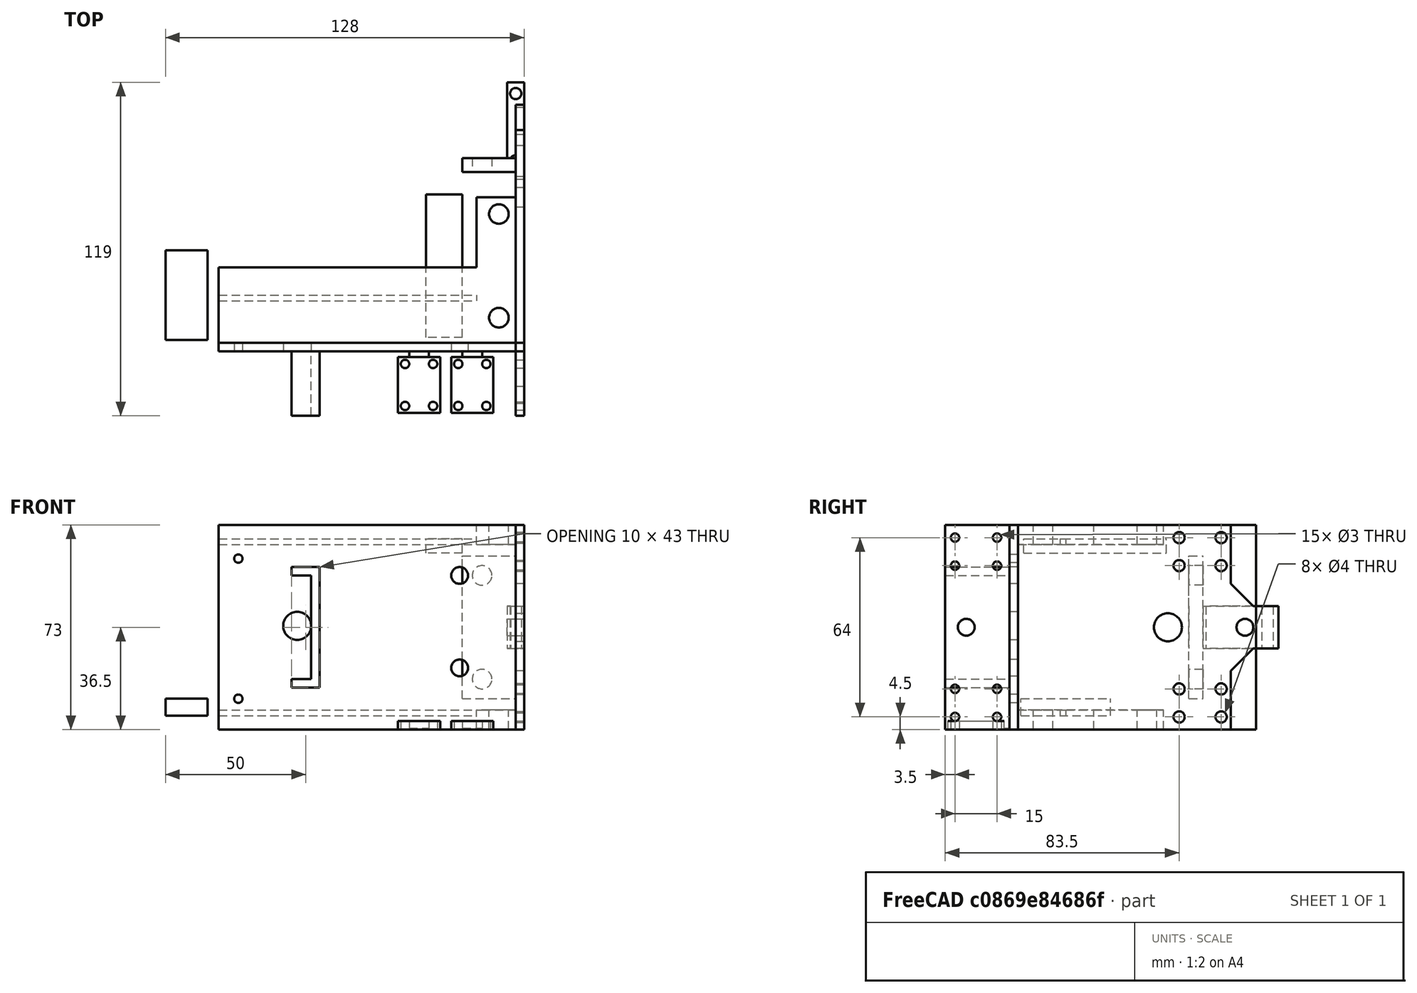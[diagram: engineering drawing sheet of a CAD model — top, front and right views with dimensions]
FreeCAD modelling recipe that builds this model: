
FCSTD DOCUMENT  (FreeCAD 0.16R6703 (Git))
Label: print
License: All rights reserved
LicenseURL: http://en.wikipedia.org/wiki/All_rights_reserved
objects: Part::Cut×48, Part::Cylinder×46, Part::Box×23, Part::MultiFuse×15
note: 132 computed .brp shape members not serialized (recipe doc carries the construction recipe); baked Part::Feature solids carry a one-line shape summary decoded from their .brp

FEATURE [Part::Box] Box001  label="Cube001"
  Height = 73
  Length = 133
  Placement = pos=(-4.99998,-4,-4.99998) rot=(0,0,1;0rad)
  Width = 3
FEATURE [Part::Box] Box005  label="Cube005"
  Height = 7
  Length = 113
  Placement = pos=(0,-4,-5) rot=(0,0,1;0rad)
  Width = 30
FEATURE [Part::Box] Box006  label="Cube006"
  Height = 7
  Length = 113
  Placement = pos=(0,-4,61) rot=(0,0,1;0rad)
  Width = 30
FEATURE [Part::Box] Box007  label="Cube007"
  Height = 2
  Length = 113
  Placement = pos=(0,14,0) rot=(0,0,1;0rad)
  Width = 2
FEATURE [Part::Box] Box008  label="Cube008"
  Height = 2
  Length = 113
  Placement = pos=(0,14,61) rot=(0,0,1;0rad)
  Width = 2
FEATURE [Part::Cut] Cut
  Base = -> Box006
  Tool = -> Box008
FEATURE [Part::Cut] Cut001
  Base = -> Box005
  Tool = -> Box007
FEATURE [Part::Box] Box009  label="Cube009"
  Height = 7
  Length = 55
  Placement = pos=(128,-4,61) rot=(0,0,1;1.5708rad)
  Width = 17
FEATURE [Part::Box] Box013  label="Cube013"
  Height = 7
  Length = 55
  Placement = pos=(128,-4,-5) rot=(0,0,1;1.5708rad)
  Width = 17
FEATURE [Part::Cylinder] Cylinder013
  Angle = 360
  Height = 3
  Placement = pos=(105,-1,50) rot=(1,0,0;1.5708rad)
  Radius = 3
FEATURE [Part::Cylinder] Cylinder015
  Angle = 360
  Height = 3
  Placement = pos=(105,-1,17) rot=(1,0,0;1.5708rad)
  Radius = 3
FEATURE [Part::Cut] Cut014
  Base = -> Box001
  Tool = -> Cylinder013
FEATURE [Part::Cut] Cut015
  Base = -> Cut014
  Tool = -> Cylinder015
FEATURE [Part::Cylinder] Cylinder016
  Angle = 360
  Height = 4
  Placement = pos=(118,-20,63) rot=(0,1,0;1.5708rad)
  Radius = 1.5
FEATURE [Part::Cut] Cut017
  Base = -> Cut015
  Tool = -> Cylinder016
FEATURE [Part::Box] Box  label="Cube"
  Height = 6
  Length = 15
  Width = 32
FEATURE [Part::Box] Box014  label="main_base"
  Height = 73
  Length = 111
  Placement = pos=(128,-27,-5) rot=(0,0,1;1.5708rad)
  Width = 3
FEATURE [Part::Box] Box016  label="Cube016"
  Height = 15
  Length = 20
  Placement = pos=(147,-26,51) rot=(0,0,1;1.5708rad)
  Width = 3
FEATURE [Part::Cylinder] Cylinder
  Angle = 360
  Height = 3
  Placement = pos=(125,-8.5,-0.5) rot=(0,1,0;1.5708rad)
  Radius = 1.5
FEATURE [Part::Cylinder] Cylinder017
  Angle = 360
  Height = 3
  Placement = pos=(125,-8.5,9.5) rot=(0,1,0;1.5708rad)
  Radius = 1.5
FEATURE [Part::Cylinder] Cylinder018
  Angle = 360
  Height = 3
  Placement = pos=(125,-23.5,9.5) rot=(0,1,0;1.5708rad)
  Radius = 1.5
FEATURE [Part::Cylinder] Cylinder019
  Angle = 360
  Height = 3
  Placement = pos=(125,-23.5,-0.5) rot=(0,1,0;1.5708rad)
  Radius = 1.5
FEATURE [Part::Cylinder] Cylinder020
  Angle = 360
  Height = 3
  Placement = pos=(125,-8.5,63.5) rot=(0,1,0;1.5708rad)
  Radius = 1.5
FEATURE [Part::Cylinder] Cylinder021
  Angle = 360
  Height = 3
  Placement = pos=(125,-23.5,53.5) rot=(0,1,0;1.5708rad)
  Radius = 1.5
FEATURE [Part::Cylinder] Cylinder022
  Angle = 360
  Height = 3
  Placement = pos=(125,-8.5,53.5) rot=(0,1,0;1.5708rad)
  Radius = 1.5
FEATURE [Part::Cylinder] Cylinder023
  Angle = 360
  Height = 3
  Placement = pos=(144,-23.5,63.5) rot=(0,1,0;1.5708rad)
  Radius = 1.5
FEATURE [Part::Cylinder] Cylinder024
  Angle = 360
  Height = 3
  Placement = pos=(125,-23.5,63.5) rot=(0,1,0;1.5708rad)
  Radius = 1.5
FEATURE [Part::Cylinder] Cylinder025
  Angle = 360
  Height = 3
  Placement = pos=(144,-8.5,63.5) rot=(0,1,0;1.5708rad)
  Radius = 1.5
FEATURE [Part::Cylinder] Cylinder026
  Angle = 360
  Height = 3
  Placement = pos=(144,-23.5,53.5) rot=(0,1,0;1.5708rad)
  Radius = 1.5
FEATURE [Part::Cylinder] Cylinder027
  Angle = 360
  Height = 3
  Placement = pos=(144,-8.5,53.5) rot=(0,1,0;1.5708rad)
  Radius = 1.5
FEATURE [Part::Cut] Cut018
  Base = -> Box016
  Tool = -> Cylinder027
FEATURE [Part::Cut] Cut019
  Base = -> Cut018
  Tool = -> Cylinder026
FEATURE [Part::Cut] Cut020
  Base = -> Cut019
  Tool = -> Cylinder025
FEATURE [Part::Cut] Cut021  label="motor_mount1"
  Base = -> Cut020
  Placement = pos=(32,0,142) rot=(0,1,0;1.5708rad)
  Tool = -> Cylinder023
FEATURE [Part::Box] Box017  label="Cube017"
  Height = 15
  Length = 20
  Placement = pos=(147,-26,51) rot=(0,0,1;1.5708rad)
  Width = 3
FEATURE [Part::Cylinder] Cylinder028
  Angle = 360
  Height = 3
  Placement = pos=(144,-23.5,63.5) rot=(0,1,0;1.5708rad)
  Radius = 1.5
FEATURE [Part::Cylinder] Cylinder029
  Angle = 360
  Height = 3
  Placement = pos=(144,-8.5,63.5) rot=(0,1,0;1.5708rad)
  Radius = 1.5
FEATURE [Part::Cylinder] Cylinder030
  Angle = 360
  Height = 3
  Placement = pos=(144,-23.5,53.5) rot=(0,1,0;1.5708rad)
  Radius = 1.5
FEATURE [Part::Cylinder] Cylinder031
  Angle = 360
  Height = 3
  Placement = pos=(144,-8.5,53.5) rot=(0,1,0;1.5708rad)
  Radius = 1.5
FEATURE [Part::Cut] Cut022
  Base = -> Box017
  Tool = -> Cylinder031
FEATURE [Part::Cut] Cut023
  Base = -> Cut022
  Tool = -> Cylinder030
FEATURE [Part::Cut] Cut024
  Base = -> Cut023
  Tool = -> Cylinder029
FEATURE [Part::Cut] Cut026
  Base = -> Box014
  Tool = -> Cylinder
FEATURE [Part::Cut] Cut027
  Base = -> Cut026
  Tool = -> Cylinder017
FEATURE [Part::Cut] Cut028
  Base = -> Cut027
  Tool = -> Cylinder018
FEATURE [Part::Cut] Cut029
  Base = -> Cut028
  Tool = -> Cylinder019
FEATURE [Part::Cut] Cut030
  Base = -> Cut029
  Tool = -> Cylinder020
FEATURE [Part::Box] Box018  label="Cube018"
  Height = 43
  Length = 32
  Placement = pos=(55,-33,10) rot=(0,0,1;1.5708rad)
  Width = 10
FEATURE [Part::Box] Box019  label="Cube019"
  Height = 37
  Length = 29
  Placement = pos=(52,-30,13) rot=(0,0,1;1.5708rad)
  Width = 7
FEATURE [Part::Cylinder] Cylinder032
  Angle = 360
  Height = 3
  Placement = pos=(26,-1,6) rot=(1,0,0;1.5708rad)
  Radius = 1.5
FEATURE [Part::Cylinder] Cylinder033
  Angle = 360
  Height = 3
  Placement = pos=(26,-1,56) rot=(1,0,0;1.5708rad)
  Radius = 1.5
FEATURE [Part::Cut] Cut035
  Base = -> Cut017
  Tool = -> Cylinder033
FEATURE [Part::Cut] Cut036  label="chassi_back"
  Base = -> Cut035
  Tool = -> Cylinder032
FEATURE [Part::Box] Box022  label="Cube022"
  Height = 6
  Length = 15
  Width = 32
FEATURE [Part::Cylinder] Cylinder035
  Angle = 360
  Height = 18
  Placement = pos=(0,4,3) rot=(0,1,0;1.5708rad)
  Radius = 2
FEATURE [Part::Cylinder] Cylinder036
  Angle = 360
  Height = 18
  Placement = pos=(0,28,3) rot=(0,1,0;1.5708rad)
  Radius = 2
FEATURE [Part::Cut] Cut039
  Base = -> Box022
  Tool = -> Cylinder035
FEATURE [Part::Cut] Cut040
  Base = -> Cut039
  Placement = pos=(122,60,39) rot=(0,1,0;1.5708rad)
  Tool = -> Cylinder036
FEATURE [Part::MultiFuse] Fusion  label="right_mount"
  Shapes = -> [Cut,Box009]
FEATURE [Part::MultiFuse] Fusion001  label="left_mount"
  Shapes = -> [Cut001,Box013]
FEATURE [Part::Cylinder] Cylinder037
  Angle = 360
  Height = 3
  Placement = pos=(125,-16,21) rot=(0,1,0;1.5708rad)
  Radius = 4
FEATURE [Part::Cylinder] Cylinder038
  Angle = 360
  Height = 3
  Placement = pos=(125,-16,38) rot=(0,1,0;1.5708rad)
  Radius = 4
FEATURE [Part::Cut] Cut041
  Tool = -> Cylinder037
FEATURE [Part::Cut] Cut042
  Base = -> Cut041
  Tool = -> Cylinder038
FEATURE [Part::Cylinder] Cylinder039
  Angle = 360
  Height = 6
  Placement = pos=(122,80,31.5) rot=(0,1,0;1.5708rad)
  Radius = 3
FEATURE [Part::Cut] Cut034  label="battery_holder"
  Base = -> Box018
  Tool = -> Box019
FEATURE [Part::Cylinder] Cylinder040
  Angle = 360
  Height = 3
  Placement = pos=(47,-1,32) rot=(1,0,0;1.5708rad)
  Radius = 5
FEATURE [Part::Cut] Cut044  label="chassi_back001"
  Base = -> Cut036
  Tool = -> Cylinder040
FEATURE [Part::Cylinder] Cylinder041
  Angle = 360
  Height = 7
  Placement = pos=(119,8,61) rot=(0,0,1;0rad)
  Radius = 3.5
FEATURE [Part::Cylinder] Cylinder042
  Angle = 360
  Height = 7
  Placement = pos=(119,45,61) rot=(0,0,1;0rad)
  Radius = 3.5
FEATURE [Part::Cylinder] Cylinder043
  Angle = 360
  Height = 7
  Placement = pos=(119,8,-5) rot=(0,0,1;0rad)
  Radius = 3.5
FEATURE [Part::Cylinder] Cylinder044
  Angle = 360
  Height = 7
  Placement = pos=(119,45,-5) rot=(0,0,1;0rad)
  Radius = 3.5
FEATURE [Part::Cut] Cut045
  Base = -> Fusion
  Tool = -> Cylinder041
FEATURE [Part::Cut] Cut046  label="left_mount001"
  Base = -> Cut045
  Tool = -> Cylinder042
FEATURE [Part::Cut] Cut047
  Base = -> Fusion001
  Tool = -> Cylinder043
FEATURE [Part::Cut] Cut048  label="right_mount001"
  Base = -> Cut047
  Tool = -> Cylinder044
FEATURE [Part::Cylinder] Cylinder046
  Angle = 360
  Height = 7
  Placement = pos=(119,8,61) rot=(0,0,1;0rad)
  Radius = 3.5
FEATURE [Part::Cylinder] Cylinder047
  Angle = 360
  Height = 7
  Placement = pos=(119,45,61) rot=(0,0,1;0rad)
  Radius = 3.5
FEATURE [Part::Box] Box023  label="Cube023"
  Height = 5
  Length = 51
  Placement = pos=(106,1,58) rot=(0,0,1;1.5708rad)
  Width = 13
FEATURE [Part::Box] Box024  label="Cube024"
  Height = 5
  Length = 22
  Placement = pos=(112,1,63) rot=(0,0,1;0rad)
  Width = 51
FEATURE [Part::Cylinder] Cylinder048
  Angle = 360
  Height = 10
  Placement = pos=(119,45,58) rot=(0,0,1;0rad)
  Radius = 3.5
FEATURE [Part::Cylinder] Cylinder049
  Angle = 360
  Height = 10
  Placement = pos=(119,8,58) rot=(0,0,1;0rad)
  Radius = 3.5
FEATURE [Part::Cut] Cut049
  Base = -> Box024
  Tool = -> Cylinder048
FEATURE [Part::Cut] Cut050
  Base = -> Cut049
  Placement = pos=(-6,128,5) rot=(1,0,0;1.5708rad)
  Tool = -> Cylinder049
FEATURE [Part::MultiFuse] Fusion006
  Shapes = -> [Cut034,Cut044]
FEATURE [Part::Box] Box025  label="Cube025"
  Height = 79
  Length = 29
  Placement = pos=(-10,-4,-8) rot=(0,0,1;0rad)
  Width = 30
FEATURE [Part::Cut] Cut025  label="motor_mount2"
  Base = -> Cut024
  Placement = pos=(51,0,142) rot=(0,1,0;1.5708rad)
  Tool = -> Cylinder028
FEATURE [Part::Box] Box026  label="Cube026"
  Height = 0.5
  Length = 7
  Placement = pos=(87,-13,-5) rot=(0,0,1;0rad)
  Width = 10
FEATURE [Part::Box] Box027  label="Cube027"
  Height = 0.5
  Length = 7
  Placement = pos=(106,-13,-5) rot=(0,0,1;0rad)
  Width = 10
FEATURE [Part::MultiFuse] Fusion008  label="motor_m1"
  Shapes = -> [Cut025,Box027]
FEATURE [Part::MultiFuse] Fusion009  label="motor_m2"
  Shapes = -> [Box026,Cut021]
FEATURE [Part::MultiFuse] Fusion010
  Shapes = -> [Fusion006,Cut046]
FEATURE [Part::MultiFuse] Fusion011
  Shapes = -> [Fusion010,Cut048]
FEATURE [Part::Cut] Cut051  label="back"
  Base = -> Fusion011
  Tool = -> Box025
FEATURE [Part::MultiFuse] Fusion012
  Shapes = -> [Cut042,Cut040]
FEATURE [Part::Cut] Cut052  label="base"
  Base = -> Fusion012
  Tool = -> Cylinder039
FEATURE [Part::MultiFuse] Fusion013  label="base001"
  Shapes = -> [Cut052,Cut050]
FEATURE [Part::Box] Box028  label="Cube028"
  Height = 48
  Length = 15
  Placement = pos=(43,-37,8) rot=(0,0,1;0rad)
  Width = 10
FEATURE [Part::Cut] Cut053  label="shortened_back"
  Base = -> Cut051
  Tool = -> Box028
FEATURE [Part::MultiFuse] Fusion014
  Shapes = -> [Cut053,Fusion013]
FEATURE [Part::MultiFuse] Fusion015
  Shapes = -> [Fusion014,Fusion008]
FEATURE [Part::MultiFuse] Fusion016
  Shapes = -> [Fusion015,Fusion009]
FEATURE [Part::Cut] Cut031
  Base = -> Cut030
  Tool = -> Cylinder021
FEATURE [Part::Cut] Cut032
  Base = -> Cut031
  Tool = -> Cylinder022
FEATURE [Part::Box] Box029  label="Cube029"
  Height = 73
  Length = 3
  Placement = pos=(125,47,-5) rot=(0,0,1;0rad)
  Width = 28
FEATURE [Part::Cylinder] Cylinder051  label="m1"
  Angle = 360
  Height = 3
  Placement = pos=(125,71.5,-0.5) rot=(0,1,0;1.5708rad)
  Radius = 2
FEATURE [Part::Cylinder] Cylinder052  label="m2"
  Angle = 360
  Height = 3
  Placement = pos=(125,56.5,9.5) rot=(0,1,0;1.5708rad)
  Radius = 2
FEATURE [Part::Cylinder] Cylinder053  label="m4"
  Angle = 360
  Height = 3
  Placement = pos=(125,71.5,9.5) rot=(0,1,0;1.5708rad)
  Radius = 2
FEATURE [Part::Cylinder] Cylinder054  label="m5"
  Angle = 360
  Height = 3
  Placement = pos=(125,71.5,53.5) rot=(0,1,0;1.5708rad)
  Radius = 2
FEATURE [Part::Cylinder] Cylinder055  label="m6"
  Angle = 360
  Height = 3
  Placement = pos=(125,71.5,63.5) rot=(0,1,0;1.5708rad)
  Radius = 2
FEATURE [Part::Cylinder] Cylinder056  label="m7"
  Angle = 360
  Height = 3
  Placement = pos=(125,56.5,63.5) rot=(0,1,0;1.5708rad)
  Radius = 2
FEATURE [Part::Cylinder] Cylinder057  label="managment"
  Angle = 360
  Height = 3
  Placement = pos=(125,-19.5,31.5) rot=(0,1,0;1.5708rad)
  Radius = 3
FEATURE [Part::Cylinder] Cylinder058  label="m8"
  Angle = 360
  Height = 3
  Placement = pos=(125,56.5,53.5) rot=(0,1,0;1.5708rad)
  Radius = 2
FEATURE [Part::Cylinder] Cylinder059
  Angle = 360
  Height = 3
  Placement = pos=(125,-19.5,31.5) rot=(0,1,0;1.5708rad)
  Radius = 3
FEATURE [Part::Cylinder] Cylinder060  label="managment2"
  Angle = 360
  Height = 3
  Placement = pos=(125,52.5,31.5) rot=(0,1,0;1.5708rad)
  Radius = 5
FEATURE [Part::MultiFuse] Fusion017
  Shapes = -> [Box029,Fusion016]
FEATURE [Part::Cylinder] Cylinder061  label="m010"
  Angle = 360
  Height = 3
  Placement = pos=(125,56.5,-0.5) rot=(0,1,0;1.5708rad)
  Radius = 2
FEATURE [Part::Cut] Cut054
  Base = -> Fusion017
  Tool = -> Cylinder061
FEATURE [Part::Cut] Cut055
  Base = -> Cut054
  Tool = -> Cylinder060
FEATURE [Part::Cut] Cut056
  Base = -> Cut055
  Tool = -> Cylinder058
FEATURE [Part::Cut] Cut057
  Base = -> Cut056
  Tool = -> Cylinder057
FEATURE [Part::Cut] Cut058
  Base = -> Cut057
  Tool = -> Cylinder056
FEATURE [Part::Cut] Cut059
  Base = -> Cut058
  Tool = -> Cylinder055
FEATURE [Part::Cut] Cut060
  Base = -> Cut059
  Tool = -> Cylinder054
FEATURE [Part::Cut] Cut061
  Base = -> Cut060
  Tool = -> Cylinder053
FEATURE [Part::Cut] Cut062
  Base = -> Cut061
  Tool = -> Cylinder052
FEATURE [Part::Cut] Cut063
  Base = -> Cut062
  Tool = -> Cylinder051
FEATURE [Part::Box] Box030  label="Cube030"
  Height = 10
  Length = 3
  Placement = pos=(125,-21,16) rot=(0,0,1;0rad)
  Width = 10
FEATURE [Part::Box] Box031  label="Cube031"
  Height = 10
  Length = 3
  Placement = pos=(125,-21,33) rot=(0,0,1;0rad)
  Width = 10
FEATURE [Part::MultiFuse] Fusion018
  Shapes = -> [Cut063,Box030]
FEATURE [Part::MultiFuse] Fusion019
  Shapes = -> [Box031,Fusion018]
FEATURE [Part::Cut] Cut064
  Base = -> Fusion019
  Tool = -> Cylinder059
